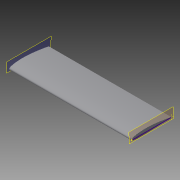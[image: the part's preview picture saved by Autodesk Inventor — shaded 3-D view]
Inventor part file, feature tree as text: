
AUTODESK INVENTOR PART (.ipt)
format: ipt  version: 2015 (Build 190159000, 159)  size: 91,648 bytes
history: native  units: in
note: dims shown in document units (in); Inventor stores cm internally (conversion verified against a paired STEP export)
features: plane x3, sketch x2, extrude x1, mirror x1
ambient origin geometry x8: Origin, YZ Plane, XZ Plane, XY Plane, X Axis, Y Axis, Z Axis, Center Point
bodies: Solid1 (feature_tree)
feature tree (7):
  extrude  "Extrusion1"  [1 undecoded]
  sketch  "Sketch2"
  plane  "Work Plane1"
  plane  "Work Plane2"
  mirror  "Mirror1"
  sketch  "Sketch1"  dims[d0=33.8583in d1=0.0in d2=-0.0137in]
  plane  "Work Plane3"
note: 1 required parameter value undecoded (feature->parameter linkage not recoverable at this tier; creation-order binding heuristic only, values carry confidence <= 0.55)
